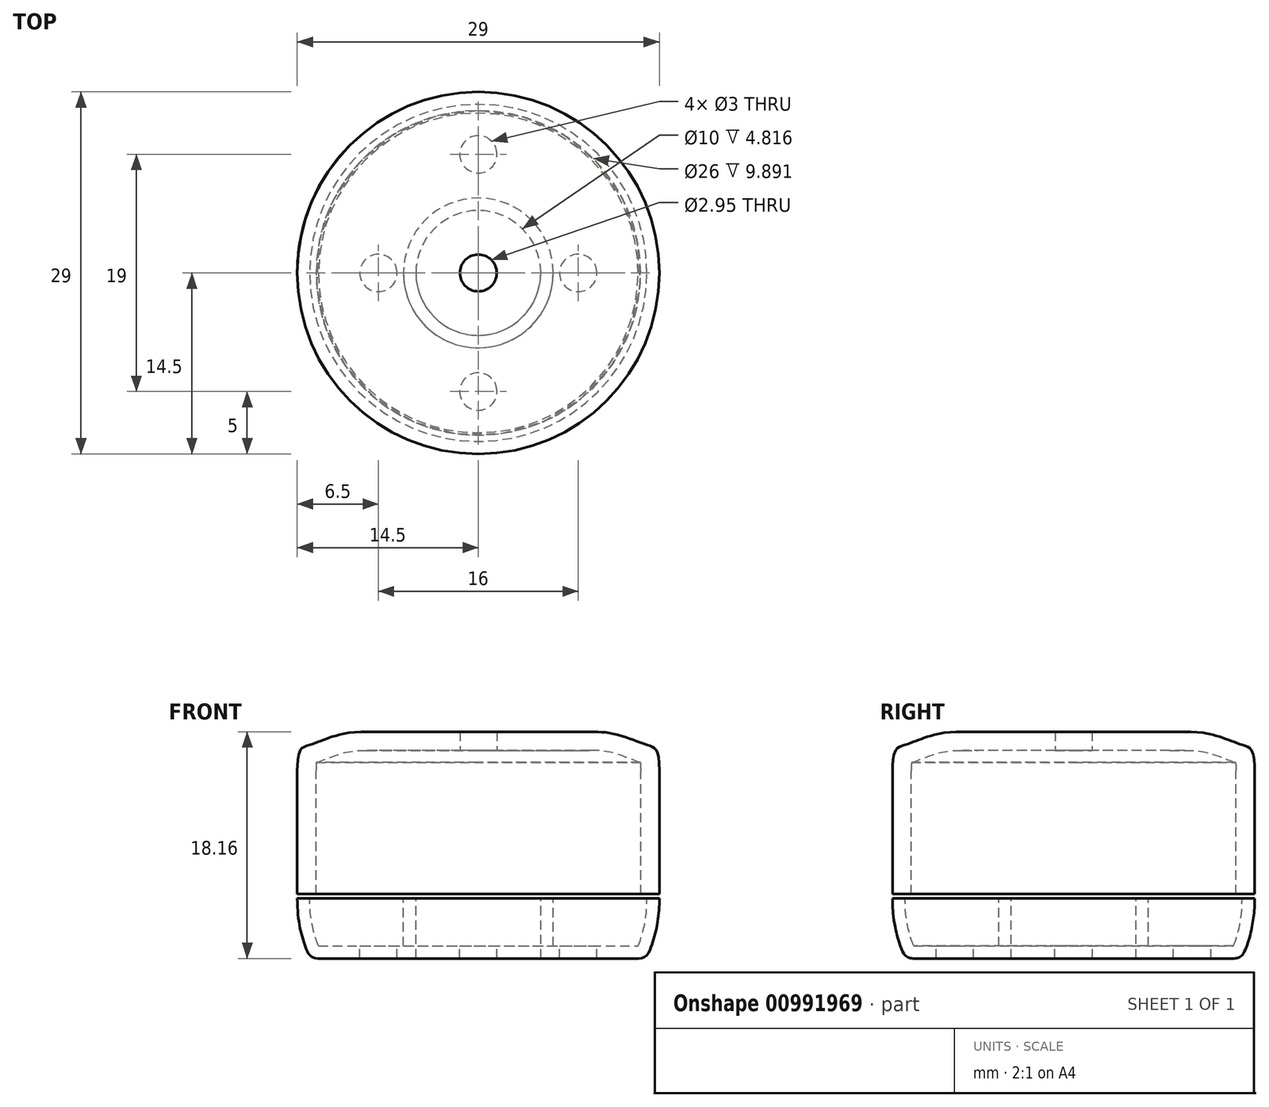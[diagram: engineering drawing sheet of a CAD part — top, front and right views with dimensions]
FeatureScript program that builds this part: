
annotation { "Feature Type Name" : "Feature", "Feature Type Description" : "" }
export const myFeature = defineFeature(function(context is Context, id is Id, definition is map)
    precondition{}
    {
        {
            var Q0;
            Q0=qCreatedBy(makeId("Right.planeOp"),FACE);
            var sketch = newSketch(context, id + "F0", { "sketchPlane" : qUnion([Q0])});
            skLineSegment(sketch, "E0", {"start": v(0, 0) * mm, "end": v(12.85, 0) * mm});
            skLineSegment(sketch, "E1", {"start": v(14.5, 0) * mm, "end": v(14.5, 13) * mm, "construction": true});
            skFitSpline(sketch, "E2", {"points": [v(12.85, 0) * mm, v(13.92, 1.14) * mm, v(14.5, 4.82) * mm], "startDerivative": vector(5.05, 0) * mm, "endDerivative": vector(0, 8.34) * mm});
            skLineSegment(sketch, "E3", {"start": v(0, 0) * mm, "end": v(0, 32.26) * mm, "construction": true});
            skLineSegment(sketch, "E4", {"start": v(14.5, 4.82) * mm, "end": v(0, 4.82) * mm});
            skLineSegment(sketch, "E5", {"start": v(0, 4.82) * mm, "end": v(0, 0) * mm});
            skSolve(sketch);
        }
        {
            var Q0;
            Q0 = qSketchRegion(id + "F0", true);
            var Q1;
            Q1=sQuery(id+"F0.wireOp",EDGE,"E0");
            var Q2;
            Q2=sQuery(id+"F0.wireOp",EDGE,"E2");
            var Q3;
            Q3=sQuery(id+"F0.wireOp",EDGE,"E4");
            var Q4;
            Q4=sQuery(id+"F0.wireOp",EDGE,"E3");
            revolve(context, id + "F1", {"surfaceOperationType" : NewSurfaceOperationType.NEW, "entities" : qUnion([Q0]), "surfaceEntities" : qUnion([Q1, Q2, Q3]), "axis" : qUnion([Q4]), "revolveType" : RevolveType.FULL});
        }
        {
            var Q0;
            Q0=makeQuery(id+"F1.opRevolve","SWEPT_FACE",FACE,{"disambiguationData":[OSD([sQuery(id+"F0.wireOp",EDGE,"E4")])]});
            var sketch = newSketch(context, id + "F2", { "sketchPlane" : qUnion([Q0])});
            skCircle(sketch, "E6", {"center": v(0, 0) * mm, "radius": 5 * mm});
            skSolve(sketch);
        }
        {
            var Q0;
            Q0=qCreatedBy(makeId("Top.planeOp"),FACE);
            var sketch = newSketch(context, id + "F3", { "sketchPlane" : qUnion([Q0])});
            skCircle(sketch, "E7", {"center": v(0, 9.5) * mm, "radius": 1.5 * mm});
            skCircle(sketch, "E8.MirrorC", {"center": v(0, -9.5) * mm, "radius": 1.5 * mm});
            skCircle(sketch, "E9", {"center": v(-8, 0) * mm, "radius": 1.5 * mm});
            skCircle(sketch, "E10.MirrorC", {"center": v(8, 0) * mm, "radius": 1.5 * mm});
            skSolve(sketch);
        }
        {
            var Q0;
            Q0=makeQuery(id+"F2.imprint","IMPRINT",FACE,{"disambiguationData":[TD([[makeQuery(id+"F2.imprint","IMPRINT",EDGE,{"derivedFrom":sQuery(id+"F2.wireOp",EDGE,"E6")}),1.0]])]});
            extrude(context, id + "F4", {"entities" : qUnion([Q0]), "operationType" : NewBodyOperationType.REMOVE, "oppositeDirection" : true, "depth" : 25 * mm, "offsetDistance" : 25 * mm});
        }
        {
            var Q0;
            Q0=makeQuery(id+"F1.opRevolve","SWEPT_FACE",FACE,{"disambiguationData":[OSD([sQuery(id+"F0.wireOp",EDGE,"E4")])]});
            shell(context, id + "F5", {"entities" : qUnion([Q0]), "thickness" : 1 * mm});
        }
        {
            var Q0;
            Q0 = qSketchRegion(id + "F3", true);
            extrude(context, id + "F6", {"entities" : qUnion([Q0]), "operationType" : NewBodyOperationType.REMOVE, "oppositeDirection" : true, "depth" : 25 * mm, "offsetDistance" : 25 * mm, "symmetric" : true});
        }
        {
            var Q0;
            Q0=qCreatedBy(makeId("Right.planeOp"),FACE);
            var sketch = newSketch(context, id + "F7", { "sketchPlane" : qUnion([Q0])});
            skLineSegment(sketch, "E11", {"start": v(0, 5.15) * mm, "end": v(14.5, 5.15) * mm});
            skLineSegment(sketch, "E12", {"start": v(14.5, 5.15) * mm, "end": v(14.5, 15.05) * mm});
            skLineSegment(sketch, "E13", {"start": v(0, 18.15) * mm, "end": v(7.7, 18.15) * mm});
            skFitSpline(sketch, "E14", {"points": [v(7.7, 18.15) * mm, v(10.9, 17.98) * mm, v(13.53, 17.09) * mm, v(14.5, 15.05) * mm], "startDerivative": vector(11.1, 0) * mm, "endDerivative": vector(0, -18.13) * mm});
            skLineSegment(sketch, "E15", {"start": v(0, 18.15) * mm, "end": v(0, 5.15) * mm});
            skSolve(sketch);
        }
        {
            var Q0;
            Q0=makeQuery(id+"F7.imprint","IMPRINT",FACE,{"disambiguationData":[TD([[makeQuery(id+"F7.imprint","IMPRINT",EDGE,{"derivedFrom":sQuery(id+"F7.wireOp",EDGE,"E11")}),1.0]])]});
            var Q1;
            Q1=sQuery(id+"F7.wireOp",EDGE,"E15");
            revolve(context, id + "F8", {"surfaceOperationType" : NewSurfaceOperationType.NEW, "entities" : qUnion([Q0]), "axis" : qUnion([Q1]), "revolveType" : RevolveType.FULL});
        }
        {
            var Q0;
            Q0=makeQuery(id+"F8.opRevolve","SWEPT_FACE",FACE,{"disambiguationData":[OSD([sQuery(id+"F7.wireOp",EDGE,"E11")])]});
            shell(context, id + "F9", {"entities" : qUnion([Q0]), "thickness" : 1.5 * mm});
        }
        {
            var Q0;
            Q0=qCreatedBy(makeId("Top.planeOp"),FACE);
            var sketch = newSketch(context, id + "F10", { "sketchPlane" : qUnion([Q0])});
            skCircle(sketch, "E16", {"center": v(0, 0) * mm, "radius": 1.48 * mm});
            skSolve(sketch);
        }
        {
            var Q0;
            Q0 = qSketchRegion(id + "F10", true);
            extrude(context, id + "F11", {"entities" : qUnion([Q0]), "operationType" : NewBodyOperationType.REMOVE, "depth" : 24.9 * mm, "offsetDistance" : 25 * mm});
        }
    });
